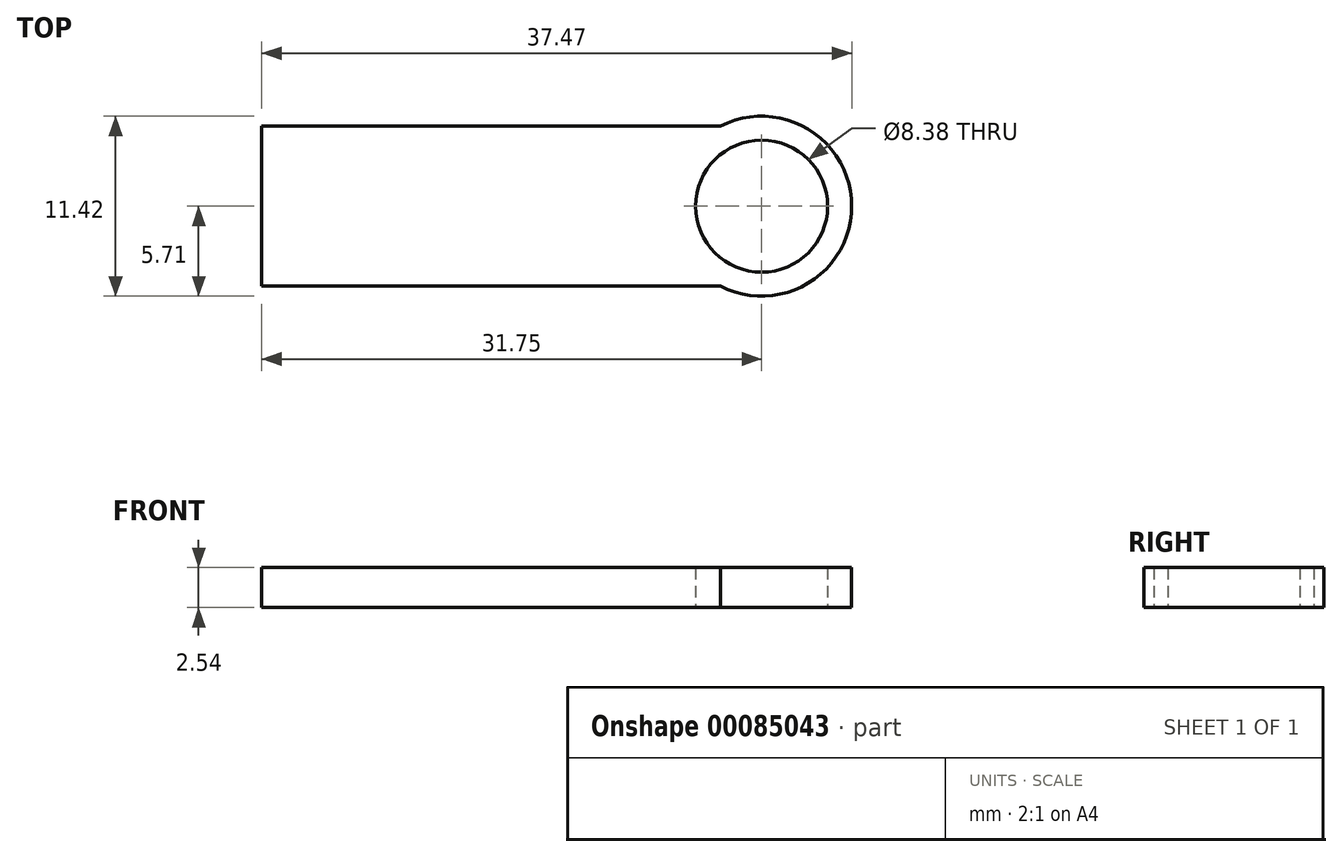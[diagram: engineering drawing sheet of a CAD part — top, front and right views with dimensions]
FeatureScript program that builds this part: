
annotation { "Feature Type Name" : "Feature", "Feature Type Description" : "" }
export const myFeature = defineFeature(function(context is Context, id is Id, definition is map)
    precondition{}
    {
        {
            var Q0;
            Q0=qCreatedBy(makeId("Top.planeOp"),FACE);
            var sketch = newSketch(context, id + "F0", { "sketchPlane" : qUnion([Q0])});
            skLineSegment(sketch, "E0.bottom", {"start": v(0, 0) * mm, "end": v(31.75, 0) * mm});
            skLineSegment(sketch, "E0.top", {"start": v(0, 10.16) * mm, "end": v(31.75, 10.16) * mm});
            skLineSegment(sketch, "E0.left", {"start": v(0, 0) * mm, "end": v(0, 10.16) * mm});
            skLineSegment(sketch, "E0.right", {"start": v(31.75, 0) * mm, "end": v(31.75, 0.89) * mm});
            skCircle(sketch, "E1", {"center": v(31.75, 5.08) * mm, "radius": 4.2 * mm});
            skCircle(sketch, "E2", {"center": v(31.75, 5.08) * mm, "radius": 5.72 * mm});
            skLineSegment(sketch, "E3.trimOffspring", {"start": v(31.75, 9.27) * mm, "end": v(31.75, 10.16) * mm});
            skSolve(sketch);
        }
        {
            var Q0;
            Q0 = qSketchRegion(id + "F0", true);
            extrude(context, id + "F1", {"entities" : qUnion([Q0]), "depth" : 2.54 * mm});
        }
    });
